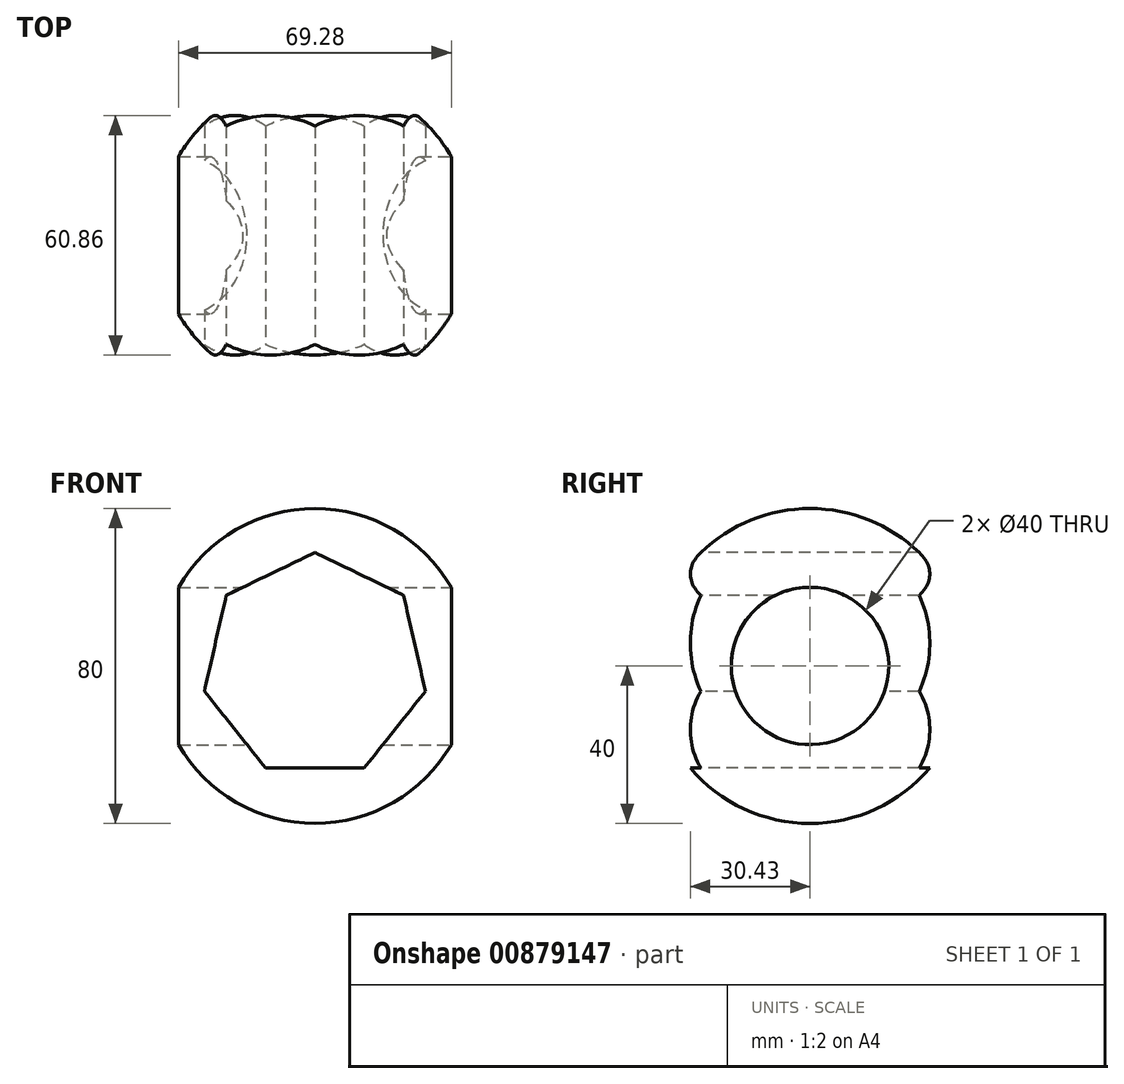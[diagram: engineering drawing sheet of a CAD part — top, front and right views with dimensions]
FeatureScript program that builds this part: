
annotation { "Feature Type Name" : "Feature", "Feature Type Description" : "" }
export const myFeature = defineFeature(function(context is Context, id is Id, definition is map)
    precondition{}
    {
        {
            var Q0;
            Q0=qCreatedBy(makeId("Front.planeOp"),FACE);
            var sketch = newSketch(context, id + "F0", { "sketchPlane" : qUnion([Q0])});
            skLineSegment(sketch, "E0", {"start": v(0, -40) * mm, "end": v(0, 40) * mm});
            skArc(sketch, "E1", {"start": v(0, 40) * mm, "mid": v(-40, 0) * mm, "end": v(0, -40) * mm});
            skSolve(sketch);
        }
        {
            var Q0;
            Q0 = qSketchRegion(id + "F0", true);
            var Q1;
            Q1=sQuery(id+"F0.wireOp",EDGE,"E0");
            revolve(context, id + "F1", {"surfaceOperationType" : NewSurfaceOperationType.NEW, "entities" : qUnion([Q0]), "axis" : qUnion([Q1]), "revolveType" : RevolveType.FULL});
        }
        {
            var Q0;
            Q0=qCreatedBy(makeId("Front.planeOp"),FACE);
            var sketch = newSketch(context, id + "F2", { "sketchPlane" : qUnion([Q0])});
            skCircle(sketch, "E2.cCircle", {"center": v(0, 0) * mm, "radius": 25.96 * mm, "construction": true});
            skLineSegment(sketch, "E2.0", {"start": v(28.09, -6.41) * mm, "end": v(12.5, -25.96) * mm});
            skLineSegment(sketch, "E2.1", {"start": v(12.5, -25.96) * mm, "end": v(-12.5, -25.96) * mm});
            skLineSegment(sketch, "E2.2", {"start": v(-12.5, -25.96) * mm, "end": v(-28.09, -6.41) * mm});
            skLineSegment(sketch, "E2.3", {"start": v(-28.09, -6.41) * mm, "end": v(-22.52, 17.96) * mm});
            skLineSegment(sketch, "E2.4", {"start": v(-22.52, 17.96) * mm, "end": v(0, 28.8) * mm});
            skLineSegment(sketch, "E2.5", {"start": v(0, 28.8) * mm, "end": v(22.52, 17.96) * mm});
            skLineSegment(sketch, "E2.6", {"start": v(22.52, 17.96) * mm, "end": v(28.09, -6.41) * mm});
            skPoint(sketch, "E2.0.midPoint", {"position": v(20.3, -16.18) * mm});
            skSolve(sketch);
        }
        {
            var Q0;
            Q0 = qSketchRegion(id + "F2", true);
            extrude(context, id + "F3", {"entities" : qUnion([Q0]), "operationType" : NewBodyOperationType.REMOVE, "endBound" : BoundingType.THROUGH_ALL, "oppositeDirection" : true, "depth" : 25 * mm, "offsetDistance" : 25 * mm, "hasSecondDirection" : true, "secondDirectionBound" : SecondDirectionBoundingType.THROUGH_ALL, "secondDirectionOppositeDirection" : false, "secondDirectionDepth" : 25 * mm});
        }
        {
            var Q0;
            Q0=qCreatedBy(makeId("Right.planeOp"),FACE);
            var sketch = newSketch(context, id + "F4", { "sketchPlane" : qUnion([Q0])});
            skCircle(sketch, "E3", {"center": v(0, 0) * mm, "radius": 20 * mm});
            skSolve(sketch);
        }
        {
            var Q0;
            Q0 = qSketchRegion(id + "F4", true);
            extrude(context, id + "F5", {"entities" : qUnion([Q0]), "operationType" : NewBodyOperationType.REMOVE, "endBound" : BoundingType.THROUGH_ALL, "oppositeDirection" : true, "depth" : 25 * mm, "offsetDistance" : 25 * mm, "hasSecondDirection" : true, "secondDirectionBound" : SecondDirectionBoundingType.THROUGH_ALL, "secondDirectionOppositeDirection" : false, "secondDirectionDepth" : 25 * mm});
        }
    });
